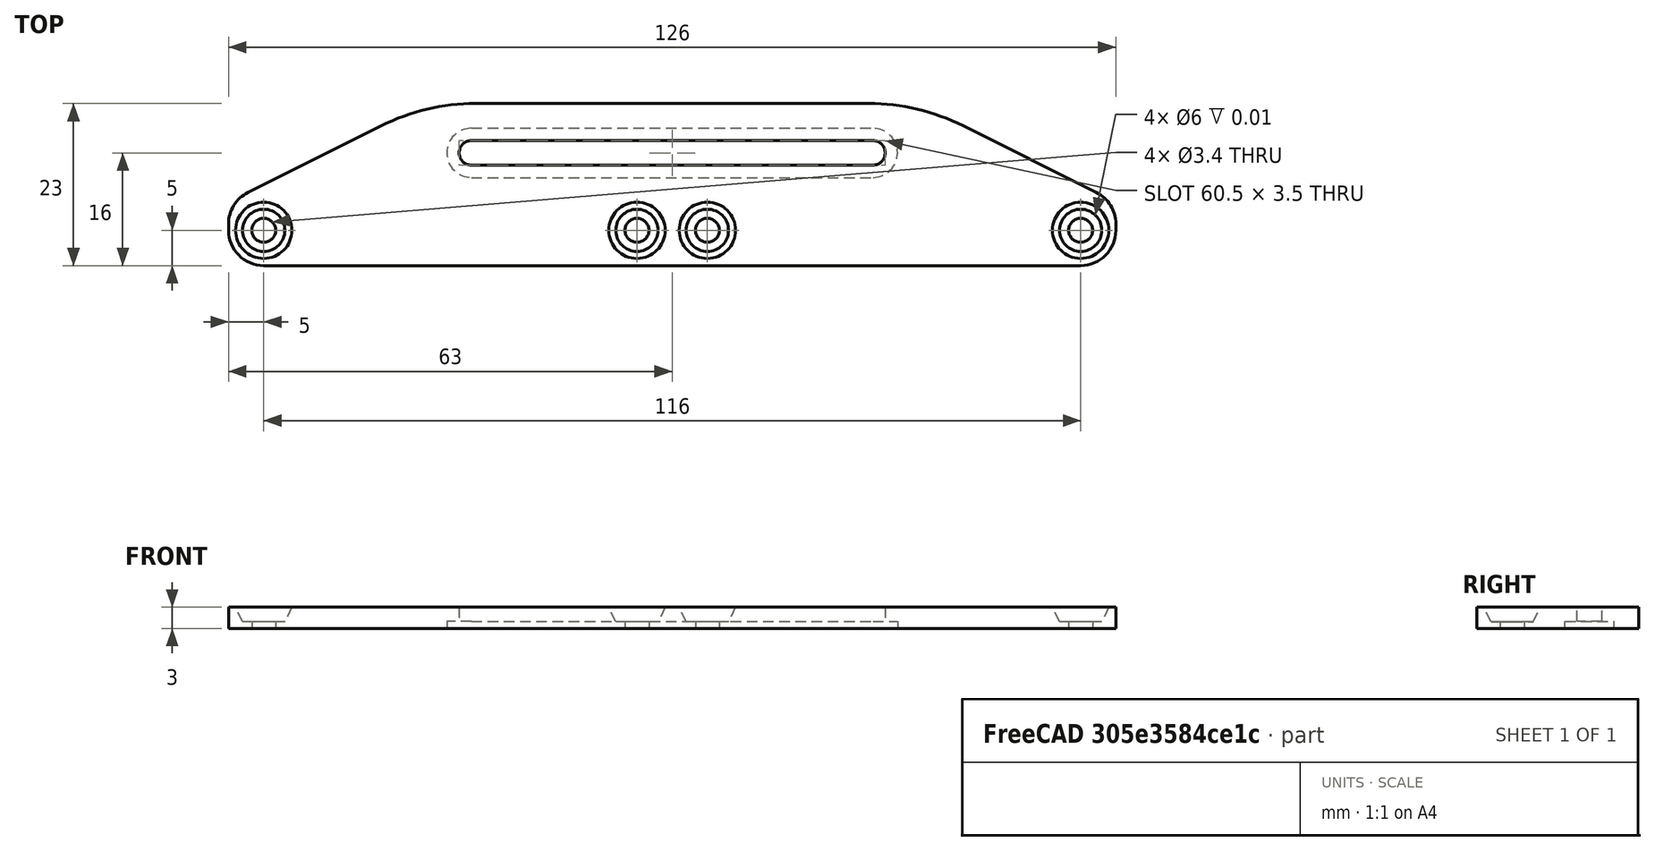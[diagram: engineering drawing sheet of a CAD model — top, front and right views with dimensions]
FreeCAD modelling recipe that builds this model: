
FCSTD DOCUMENT  (FreeCAD 0.19R24366 (Git))
Label: fractal_nexus_9pslim_frame
License: All rights reserved
LicenseURL: http://en.wikipedia.org/wiki/All_rights_reserved
objects: TechDraw::DrawViewDimension×13, Sketcher::SketchObject×3, PartDesign::Chamfer×3, PartDesign::Fillet×3, TechDraw::DrawViewPart×3, PartDesign::Pocket×2, PartDesign::AdditiveBox×1, PartDesign::Hole×1, PartDesign::Body×1, TechDraw::DrawSVGTemplate×1, TechDraw::DrawPage×1
note: 24 computed .brp shape members not serialized (recipe doc carries the construction recipe); baked Part::Feature solids carry a one-line shape summary decoded from their .brp

FEATURE [PartDesign::AdditiveBox] Box001
  AttacherType = Attacher::AttachEngine3D
  Height = 3
  Length = 126
  Refine = true
  Width = 23
FEATURE [Sketcher::SketchObject] Sketch005
  ExternalGeometry = -> [Box001]
  FullyConstrained = false
  MapMode = 5
  Placement = pos=(0,0,3) rot=(0,0,1;0rad)
  Support = -> [Box001]
  sketch-geometry (10):
    g0: LineSegment StartX=0 StartY=0 StartZ=0 EndX=0 EndY=5 EndZ=0
    g1: LineSegment StartX=0 StartY=5 StartZ=0 EndX=5 EndY=5 EndZ=0
    g2: LineSegment StartX=0 StartY=5 StartZ=0 EndX=58 EndY=5 EndZ=0
    g3: LineSegment StartX=0 StartY=5 StartZ=0 EndX=121 EndY=5 EndZ=0
    g4: LineSegment StartX=126 StartY=0 StartZ=0 EndX=126 EndY=5 EndZ=0
    g5: LineSegment StartX=126 StartY=5 StartZ=0 EndX=68 EndY=5 EndZ=0
    g6: Circle CenterX=5 CenterY=5 CenterZ=0 NormalX=0 NormalY=0 NormalZ=1 AngleXU=0 Radius=1.67441
    g7: Circle CenterX=58 CenterY=5 CenterZ=0 NormalX=0 NormalY=0 NormalZ=1 AngleXU=0 Radius=1.65625
    g8: Circle CenterX=68 CenterY=5 CenterZ=0 NormalX=0 NormalY=0 NormalZ=1 AngleXU=0 Radius=1.85197
    g9: Circle CenterX=121 CenterY=5 CenterZ=0 NormalX=0 NormalY=0 NormalZ=1 AngleXU=0 Radius=1.9784
  constraints (22):
    c: Coincident(g0,g-1)
    c: PointOnObject(g0,g-2)
    c: DistanceY(g0,g0) = 5
    c: Coincident(g1,g0)
    c: Horizontal(g1)
    c: Coincident(g2,g0)
    c: Horizontal(g2)
    c: Coincident(g3,g0)
    c: Horizontal(g3)
    c: DistanceX(g1,g1) = 5
    c: Coincident(g4,g-3)
    c: Vertical(g4)
    c: Coincident(g5,g4)
    c: Horizontal(g5)
    c: Equal(g2,g5)
    c: Equal(g4,g0)
    c: Coincident(g6,g1)
    c: Coincident(g7,g2)
    c: Coincident(g8,g5)
    c: Coincident(g9,g3)
    c: DistanceX(g6,g7) = 53
    c: DistanceX(g6,g9) = 116
FEATURE [PartDesign::Hole] Hole003  label="Holes"
  BaseFeature = -> Box001
  Depth = 24
  DepthType = 0
  Diameter = 3.4
  DrillForDepth = false
  DrillPoint = 0
  DrillPointAngle = 360
  HoleCutCountersinkAngle = 90
  HoleCutCustomValues = true
  HoleCutDepth = 2.1
  HoleCutDiameter = 6
  HoleCutType = 6
  ModelActualThread = false
  Profile = -> Sketch005
  Refine = true
  Tapered = false
  TaperedAngle = 90
  ThreadAngle = 0
  ThreadClass = 0
  ThreadCutOffInner = 0
  ThreadCutOffOuter = 0
  ThreadDirection = 0
  ThreadFit = 0
  ThreadPitch = 0
  ThreadSize = 9
  ThreadType = 1
  Threaded = false
FEATURE [Sketcher::SketchObject] Sketch006
  ExternalGeometry = -> [Hole003]
  FullyConstrained = true
  MapMode = 5
  Placement = pos=(0,0,0) rot=(1,0,0;3.14159rad)
  Support = -> [Hole003]
  sketch-geometry (8):
    g0: ArcOfCircle CenterX=34.5 CenterY=-16 CenterZ=0 NormalX=0 NormalY=0 NormalZ=1 AngleXU=0 Radius=3.5 StartAngle=1.5708 EndAngle=4.71239
    g1: ArcOfCircle CenterX=91.5 CenterY=-16 CenterZ=0 NormalX=0 NormalY=0 NormalZ=1 AngleXU=0 Radius=3.5 StartAngle=4.71239 EndAngle=7.85398
    g2: LineSegment StartX=34.5 StartY=-19.5 StartZ=0 EndX=91.5 EndY=-19.5 EndZ=0
    g3: LineSegment StartX=34.5 StartY=-12.5 StartZ=0 EndX=91.5 EndY=-12.5 EndZ=0
    g4: LineSegment StartX=0 StartY=-23 StartZ=0 EndX=0 EndY=-16 EndZ=0
    g5: LineSegment StartX=0 StartY=-16 StartZ=0 EndX=34.5 EndY=-16 EndZ=0
    g6: LineSegment StartX=91.5 StartY=-16 StartZ=0 EndX=126 EndY=-16 EndZ=0
    g7: LineSegment StartX=126 StartY=-16 StartZ=0 EndX=126 EndY=-23 EndZ=0
  constraints (20):
    c: Tangent(g0,g3) = 1.5708
    c: Tangent(g0,g2) = -1.5708
    c: Tangent(g2,g1) = -1.5708
    c: Tangent(g3,g1) = 1.5708
    c: Horizontal(g2)
    c: Equal(g0,g1)
    c: DistanceX(g0,g1) = 57
    c: DistanceY(g1,g1) = 7
    c: Coincident(g4,g-3)
    c: PointOnObject(g4,g-2)
    c: Coincident(g5,g4)
    c: Coincident(g5,g0)
    c: Horizontal(g5)
    c: Coincident(g6,g1)
    c: Horizontal(g6)
    c: Coincident(g7,g6)
    c: Coincident(g7,g-4)
    c: Vertical(g7)
    c: Equal(g5,g6)
    c: DistanceY(g4,g4) = 7
FEATURE [PartDesign::Pocket] Pocket
  BaseFeature = -> Hole003
  Length = 1
  Length2 = 100
  Profile = -> Sketch006
  Refine = true
  Type = 0
FEATURE [Sketcher::SketchObject] Sketch007
  ExternalGeometry = -> [Pocket]
  FullyConstrained = true
  MapMode = 5
  Placement = pos=(0,0,1) rot=(1,0,0;3.14159rad)
  Support = -> [Pocket]
  sketch-geometry (4):
    g0: ArcOfCircle CenterX=34.5 CenterY=-16 CenterZ=0 NormalX=0 NormalY=0 NormalZ=1 AngleXU=0 Radius=1.75 StartAngle=1.5708 EndAngle=4.71239
    g1: ArcOfCircle CenterX=91.5 CenterY=-16 CenterZ=0 NormalX=0 NormalY=0 NormalZ=1 AngleXU=0 Radius=1.75 StartAngle=4.71239 EndAngle=7.85398
    g2: LineSegment StartX=34.5 StartY=-17.75 StartZ=0 EndX=91.5 EndY=-17.75 EndZ=0
    g3: LineSegment StartX=34.5 StartY=-14.25 StartZ=0 EndX=91.5 EndY=-14.25 EndZ=0
  constraints (8):
    c: Tangent(g0,g3) = 1.5708
    c: Tangent(g0,g2) = -1.5708
    c: Tangent(g2,g1) = -1.5708
    c: Tangent(g3,g1) = 1.5708
    c: Horizontal(g2)
    c: DistanceY(g1,g1) = 3.5
    c: Coincident(g1,g-4)
    c: Coincident(g0,g-3)
FEATURE [PartDesign::Pocket] Pocket001
  BaseFeature = -> Pocket
  Length = 5
  Length2 = 100
  Profile = -> Sketch007
  Refine = true
  Type = 0
FEATURE [PartDesign::Chamfer] Chamfer
  Angle = 45
  Base = -> Pocket001 [Edge10,Edge11,Edge12,Edge13]
  BaseFeature = -> Pocket001
  ChamferType = 1
  FlipDirection = false
  Refine = true
  Size = 1
  Size2 = 2.09
  SupportTransform = false
FEATURE [PartDesign::Fillet] Fillet001
  Base = -> Chamfer [Edge15,Edge21]
  BaseFeature = -> Chamfer
  Radius = 5
  Refine = true
  SupportTransform = false
FEATURE [PartDesign::Chamfer] Chamfer001
  Angle = 45
  Base = -> Fillet001 [Edge21]
  BaseFeature = -> Fillet001
  ChamferType = 1
  FlipDirection = false
  Refine = true
  Size = 28
  Size2 = 14
  SupportTransform = false
FEATURE [PartDesign::Chamfer] Chamfer002
  Angle = 45
  Base = -> Chamfer001 [Edge18]
  BaseFeature = -> Chamfer001
  ChamferType = 1
  FlipDirection = false
  Refine = true
  Size = 28
  Size2 = 14
  SupportTransform = false
FEATURE [PartDesign::Fillet] Fillet002
  Base = -> Chamfer002 [Edge21,Edge23]
  BaseFeature = -> Chamfer002
  Radius = 5
  Refine = true
  SupportTransform = false
FEATURE [PartDesign::Fillet] Fillet003
  Base = -> Fillet002 [Edge21,Edge25]
  BaseFeature = -> Fillet002
  Radius = 30
  Refine = true
  SupportTransform = false
FEATURE [PartDesign::Body] Body001  label="v2.1"
  Group = -> [Box001,Sketch005,Hole003,Sketch006,Pocket,Sketch007,Pocket001,Chamfer,Fillet001,Chamfer001,Chamfer002,Fillet002,Fillet003]
  Origin = -> Origin001
  Tip = -> Fillet003
FEATURE [TechDraw::DrawSVGTemplate] Template
  EditableTexts = AUTHOR_NAME=Julian G; DN=1/1; DRAWING_TITLE=fractal_nexus_9pslim_frame; FC-DATE=2022-03-03; FC-REV=v2.1; FC-SC=1; FC-SH=X / Y; FC-SI=A4; PN=1/1; SI-1=This drawing is just supplied as "nice to have",; SI-2=don't actually try to build something with this.
  Height = 297
  Orientation = 0
  Width = 210
FEATURE [TechDraw::DrawViewPart] View  label="Bottom"
  Caption = Bottom
  CoarseView = false
  Direction = (0,0,1)
  Focus = 100
  HardHidden = false
  IsoCount = 0
  IsoHidden = false
  IsoVisible = false
  LockPosition = false
  Perspective = false
  Rotation = 0
  ScaleType = 0
  SeamHidden = false
  SeamVisible = true
  SmoothHidden = false
  SmoothVisible = true
  Source = -> [Body001]
  X = 110.412
  XDirection = (-1,0,0)
  Y = 246.632
FEATURE [TechDraw::DrawViewPart] View001  label="Top"
  Caption = Top
  CoarseView = false
  Direction = (0,0,-1)
  Focus = 100
  HardHidden = false
  IsoCount = 0
  IsoHidden = false
  IsoVisible = false
  LockPosition = false
  Perspective = false
  Rotation = 0
  ScaleType = 0
  SeamHidden = false
  SeamVisible = true
  SmoothHidden = false
  SmoothVisible = true
  Source = -> [Body001]
  X = 110.466
  XDirection = (-1,0,0)
  Y = 188.715
FEATURE [TechDraw::DrawViewDimension] Dimension
  Arbitrary = false
  ArbitraryTolerances = false
  EqualTolerance = true
  FormatSpec = %.2f
  FormatSpecOverTolerance = %+.2f
  FormatSpecUnderTolerance = %+.2f
  Inverted = false
  LockPosition = false
  MeasureType = 1
  OverTolerance = 0
  References2D = -> [View001]
  Rotation = 0
  ScaleType = 0
  TheoreticalExact = false
  Type = 2
  UnderTolerance = 0
  X = -75.5987
  Y = -3.90821
FEATURE [TechDraw::DrawViewDimension] Dimension002
  Arbitrary = false
  ArbitraryTolerances = false
  EqualTolerance = true
  FormatSpec = R%.2f
  FormatSpecOverTolerance = %+.2f
  FormatSpecUnderTolerance = %+.2f
  Inverted = false
  LockPosition = false
  MeasureType = 1
  OverTolerance = 0
  References2D = -> [View001]
  Rotation = 0
  ScaleType = 0
  TheoreticalExact = false
  Type = 4
  UnderTolerance = 0
  X = 70.7588
  Y = -0.804289
FEATURE [TechDraw::DrawViewDimension] Dimension003
  Arbitrary = false
  ArbitraryTolerances = false
  EqualTolerance = true
  FormatSpec = %.2f
  FormatSpecOverTolerance = %+.2f
  FormatSpecUnderTolerance = %+.2f
  Inverted = false
  LockPosition = false
  MeasureType = 1
  OverTolerance = 0
  References2D = -> [View001]
  Rotation = 0
  ScaleType = 0
  TheoreticalExact = false
  Type = 1
  UnderTolerance = 0
  X = 0.750142
  Y = 17.5959
FEATURE [TechDraw::DrawViewDimension] Dimension004
  Arbitrary = false
  ArbitraryTolerances = false
  EqualTolerance = true
  FormatSpec = %.2f
  FormatSpecOverTolerance = %+.2f
  FormatSpecUnderTolerance = %+.2f
  Inverted = false
  LockPosition = false
  MeasureType = 1
  OverTolerance = 0
  References2D = -> [View001]
  Rotation = 0
  ScaleType = 0
  TheoreticalExact = false
  Type = 2
  UnderTolerance = 0
  X = 35.1561
  Y = -3.44987
FEATURE [TechDraw::DrawViewDimension] Dimension005
  Arbitrary = false
  ArbitraryTolerances = false
  EqualTolerance = true
  FormatSpec = %.2f
  FormatSpecOverTolerance = %+.2f
  FormatSpecUnderTolerance = %+.2f
  Inverted = false
  LockPosition = false
  MeasureType = 1
  OverTolerance = 0
  References2D = -> [View]
  Rotation = 0
  ScaleType = 0
  TheoreticalExact = false
  Type = 1
  UnderTolerance = 0
  X = 0.599514
  Y = 25.3442
FEATURE [TechDraw::DrawViewDimension] Dimension006
  Arbitrary = false
  ArbitraryTolerances = false
  EqualTolerance = true
  FormatSpec = %.2f
  FormatSpecOverTolerance = %+.2f
  FormatSpecUnderTolerance = %+.2f
  Inverted = false
  LockPosition = false
  MeasureType = 1
  OverTolerance = 0
  References2D = -> [View]
  Rotation = 0
  ScaleType = 0
  TheoreticalExact = false
  Type = 2
  UnderTolerance = 0
  X = 68.7497
  Y = 1.62031
FEATURE [TechDraw::DrawViewPart] View002  label="Left (4x Scale)"
  Caption = Left (4x Scale)
  CoarseView = false
  Direction = (-1,0,0)
  Focus = 100
  HardHidden = true
  IsoCount = 0
  IsoHidden = false
  IsoVisible = false
  LockPosition = false
  Perspective = false
  Rotation = 0
  Scale = 4
  ScaleType = 0
  SeamHidden = false
  SeamVisible = true
  SmoothHidden = false
  SmoothVisible = true
  Source = -> [Body001]
  X = 102.865
  XDirection = (0,-1,0)
  Y = 130.28
FEATURE [TechDraw::DrawViewDimension] Dimension008
  Arbitrary = false
  ArbitraryTolerances = false
  EqualTolerance = true
  FormatSpec = %.2f
  FormatSpecOverTolerance = %+.2f
  FormatSpecUnderTolerance = %+.2f
  Inverted = false
  LockPosition = false
  MeasureType = 1
  OverTolerance = 0
  References2D = -> [View002]
  Rotation = 0
  ScaleType = 0
  TheoreticalExact = false
  Type = 1
  UnderTolerance = 0
  X = 8.42712
  Y = -18.377
FEATURE [TechDraw::DrawViewDimension] Dimension009
  Arbitrary = false
  ArbitraryTolerances = false
  EqualTolerance = true
  FormatSpec = %.2f
  FormatSpecOverTolerance = %+.2f
  FormatSpecUnderTolerance = %+.2f
  Inverted = false
  LockPosition = false
  MeasureType = 1
  OverTolerance = 0
  References2D = -> [View002]
  Rotation = 0
  ScaleType = 0
  TheoreticalExact = false
  Type = 1
  UnderTolerance = 0
  X = 25.6907
  Y = 23.2125
FEATURE [TechDraw::DrawViewDimension] Dimension010
  Arbitrary = false
  ArbitraryTolerances = false
  EqualTolerance = true
  FormatSpec = %.2f
  FormatSpecOverTolerance = %+.2f
  FormatSpecUnderTolerance = %+.2f
  Inverted = false
  LockPosition = false
  MeasureType = 1
  OverTolerance = 0
  References2D = -> [View002]
  Rotation = 0
  ScaleType = 0
  TheoreticalExact = false
  Type = 1
  UnderTolerance = 0
  X = -18.4488
  Y = -28.4388
FEATURE [TechDraw::DrawViewDimension] Dimension011
  Arbitrary = false
  ArbitraryTolerances = false
  EqualTolerance = true
  FormatSpec = %.2f
  FormatSpecOverTolerance = %+.2f
  FormatSpecUnderTolerance = %+.2f
  Inverted = false
  LockPosition = false
  MeasureType = 1
  OverTolerance = 0
  References2D = -> [View002]
  Rotation = 0
  ScaleType = 0
  TheoreticalExact = false
  Type = 2
  UnderTolerance = 0
  X = -39.8896
  Y = -11.8925
FEATURE [TechDraw::DrawViewDimension] Dimension012
  Arbitrary = false
  ArbitraryTolerances = false
  EqualTolerance = true
  FormatSpec = %.2f
  FormatSpecOverTolerance = %+.2f
  FormatSpecUnderTolerance = %+.2f
  Inverted = false
  LockPosition = false
  MeasureType = 1
  OverTolerance = 0
  References2D = -> [View002]
  Rotation = 0
  ScaleType = 0
  TheoreticalExact = false
  Type = 2
  UnderTolerance = 0
  X = 49.1545
  Y = 7.59483
FEATURE [TechDraw::DrawViewDimension] Dimension013
  Arbitrary = false
  ArbitraryTolerances = false
  EqualTolerance = true
  FormatSpec = %.2f
  FormatSpecOverTolerance = %+.2f
  FormatSpecUnderTolerance = %+.2f
  Inverted = false
  LockPosition = false
  MeasureType = 1
  OverTolerance = 0
  References2D = -> [View002]
  Rotation = 0
  ScaleType = 0
  TheoreticalExact = false
  Type = 1
  UnderTolerance = 0
  X = -18.4935
  Y = -18.1457
FEATURE [TechDraw::DrawViewDimension] Dimension014
  Arbitrary = false
  ArbitraryTolerances = false
  EqualTolerance = true
  FormatSpec = R%.2f
  FormatSpecOverTolerance = %+.2f
  FormatSpecUnderTolerance = %+.2f
  Inverted = false
  LockPosition = false
  MeasureType = 1
  OverTolerance = 0
  References2D = -> [View001]
  Rotation = 0
  ScaleType = 0
  TheoreticalExact = false
  Type = 4
  UnderTolerance = 0
  X = -36.4913
  Y = 13.5182
FEATURE [TechDraw::DrawPage] Page
  KeepUpdated = true
  NextBalloonIndex = 1
  ProjectionType = 0
  Template = -> Template
  Views = -> [View,View001,Dimension,Dimension002,Dimension003,Dimension004,Dimension005,Dimension006,View002,Dimension008,Dimension009,Dimension010,Dimension011,Dimension012,Dimension013,Dimension014]
